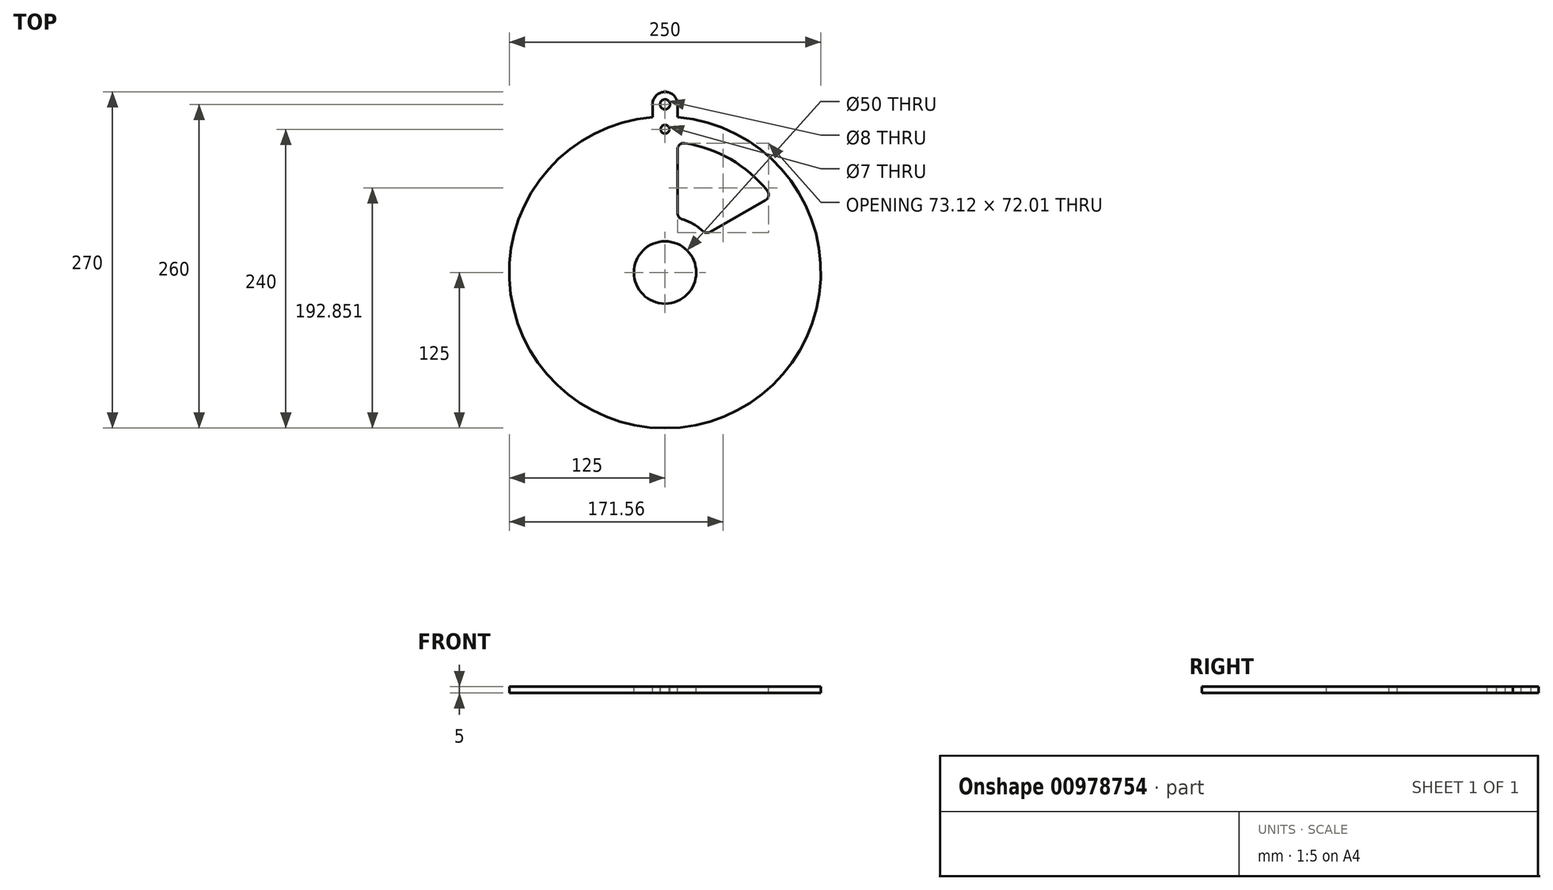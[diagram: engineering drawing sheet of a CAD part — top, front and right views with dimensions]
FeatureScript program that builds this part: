
annotation { "Feature Type Name" : "Feature", "Feature Type Description" : "" }
export const myFeature = defineFeature(function(context is Context, id is Id, definition is map)
    precondition{}
    {
        {
            var Q0;
            Q0=qCreatedBy(makeId("Top.planeOp"),FACE);
            var sketch = newSketch(context, id + "F0", { "sketchPlane" : qUnion([Q0])});
            skCircle(sketch, "E0", {"center": v(0, 0) * mm, "radius": 25 * mm});
            skSolve(sketch);
        }
        {
            var Q0;
            Q0=qCreatedBy(makeId("Top.planeOp"),FACE);
            var sketch = newSketch(context, id + "F1", { "sketchPlane" : qUnion([Q0])});
            skCircle(sketch, "E1", {"center": v(0, 0) * mm, "radius": 125 * mm});
            skSolve(sketch);
        }
        {
            var Q0;
            Q0=qCreatedBy(makeId("Top.planeOp"),FACE);
            var sketch = newSketch(context, id + "F2", { "sketchPlane" : qUnion([Q0])});
            skLineSegment(sketch, "E2", {"start": v(10, 98.87) * mm, "end": v(10, 47.7) * mm});
            skLineSegment(sketch, "E3", {"start": v(36.3, 32.5) * mm, "end": v(80.62, 58.1) * mm});
            skArc(sketch, "E4", {"start": v(82.03, 65.55) * mm, "mid": v(52.5, 90.93) * mm, "end": v(15.75, 103.81) * mm});
            skArc(sketch, "E5", {"start": v(30.43, 33.15) * mm, "mid": v(22.5, 38.97) * mm, "end": v(13.5, 42.93) * mm});
            skLineSegment(sketch, "E6", {"start": v(0, 0) * mm, "end": v(223.37, 128.96) * mm, "construction": true});
            skLineSegment(sketch, "E7", {"start": v(0, 0) * mm, "end": v(0, 140.53) * mm, "construction": true});
            skPoint(sketch, "E8.visualSharp", {"position": v(10, 104.52) * mm});
            skArc(sketch, "E8.filletArc", {"start": v(15.75, 103.81) * mm, "mid": v(11.74, 102.66) * mm, "end": v(10, 98.87) * mm});
            skPoint(sketch, "E9.visualSharp", {"position": v(85.52, 60.92) * mm});
            skArc(sketch, "E9.filletArc", {"start": v(80.62, 58.1) * mm, "mid": v(83.04, 61.5) * mm, "end": v(82.03, 65.55) * mm});
            skPoint(sketch, "E10.visualSharp", {"position": v(33, 30.6) * mm});
            skArc(sketch, "E10.filletArc", {"start": v(30.43, 33.15) * mm, "mid": v(33.26, 31.87) * mm, "end": v(36.3, 32.5) * mm});
            skPoint(sketch, "E11.visualSharp", {"position": v(10, 43.87) * mm});
            skArc(sketch, "E11.filletArc", {"start": v(10, 47.7) * mm, "mid": v(10.97, 44.74) * mm, "end": v(13.5, 42.93) * mm});
            skSolve(sketch);
        }
        {
            var Q0;
            Q0=qCreatedBy(makeId("Top.planeOp"),FACE);
            var sketch = newSketch(context, id + "F3", { "sketchPlane" : qUnion([Q0])});
            skLineSegment(sketch, "E12", {"start": v(-10, 120) * mm, "end": v(-10, 135) * mm});
            skArc(sketch, "E13", {"start": v(10, 135) * mm, "mid": v(0, 145) * mm, "end": v(-10, 135) * mm});
            skLineSegment(sketch, "E14", {"start": v(10, 135) * mm, "end": v(10, 120) * mm});
            skLineSegment(sketch, "E15", {"start": v(-10, 120) * mm, "end": v(10, 120) * mm});
            skSolve(sketch);
        }
        {
            var Q0;
            Q0=makeQuery(id+"F1.imprint","IMPRINT",FACE,{"disambiguationData":[TD([[makeQuery(id+"F1.imprint","IMPRINT",EDGE,{"derivedFrom":sQuery(id+"F1.wireOp",EDGE,"E1")}),1.0]])]});
            extrude(context, id + "F4", {"entities" : qUnion([Q0]), "oppositeDirection" : true, "depth" : 5 * mm, "offsetDistance" : 25 * mm});
        }
        {
            var Q0;
            Q0 = qSketchRegion(id + "F2", true);
            extrude(context, id + "F5", {"entities" : qUnion([Q0]), "operationType" : NewBodyOperationType.REMOVE, "endBound" : BoundingType.UP_TO_NEXT, "oppositeDirection" : true, "depth" : 25 * mm, "offsetDistance" : 25 * mm});
        }
        {
            var Q0;
            Q0=makeQuery(id+"F3.imprint","IMPRINT",FACE,{"disambiguationData":[TD([[makeQuery(id+"F3.imprint","IMPRINT",EDGE,{"derivedFrom":sQuery(id+"F3.wireOp",EDGE,"E12")}),-1.0]])]});
            var Q1;
            Q1=makeQuery(id+"F4.opExtrude","CAP_FACE",FACE,{"disambiguationData":[OSD([sQuery(id+"F1.wireOp",EDGE,"E1")])],"isStart":false});
            extrude(context, id + "F6", {"entities" : qUnion([Q0]), "operationType" : NewBodyOperationType.ADD, "endBound" : BoundingType.UP_TO_SURFACE, "oppositeDirection" : true, "depth" : 25 * mm, "endBoundEntityFace" : qUnion([Q1]), "offsetDistance" : 25 * mm});
        }
        {
            var Q0;
            Q0=makeQuery(id+"F0.imprint","IMPRINT",FACE,{"disambiguationData":[TD([[makeQuery(id+"F0.imprint","IMPRINT",EDGE,{"derivedFrom":sQuery(id+"F0.wireOp",EDGE,"E0")}),1.0]])]});
            extrude(context, id + "F7", {"entities" : qUnion([Q0]), "operationType" : NewBodyOperationType.REMOVE, "oppositeDirection" : true, "depth" : 25 * mm, "offsetDistance" : 25 * mm});
        }
        {
            var Q0;
            Q0=qCreatedBy(makeId("Top.planeOp"),FACE);
            var sketch = newSketch(context, id + "F8", { "sketchPlane" : qUnion([Q0])});
            skCircle(sketch, "E16", {"center": v(0, 135) * mm, "radius": 4 * mm});
            skSolve(sketch);
        }
        {
            var Q0;
            Q0 = qSketchRegion(id + "F8", true);
            extrude(context, id + "F9", {"entities" : qUnion([Q0]), "operationType" : NewBodyOperationType.REMOVE, "endBound" : BoundingType.UP_TO_NEXT, "oppositeDirection" : true, "depth" : 25 * mm, "offsetDistance" : 25 * mm});
        }
        {
            var Q0;
            Q0=qCreatedBy(makeId("Top.planeOp"),FACE);
            var sketch = newSketch(context, id + "F10", { "sketchPlane" : qUnion([Q0])});
            skCircle(sketch, "E17", {"center": v(0, 115) * mm, "radius": 3.5 * mm});
            skSolve(sketch);
        }
        {
            var Q0;
            Q0=makeQuery(id+"F10.imprint","IMPRINT",FACE,{"disambiguationData":[TD([[makeQuery(id+"F10.imprint","IMPRINT",EDGE,{"derivedFrom":sQuery(id+"F10.wireOp",EDGE,"E17")}),1.0]])]});
            extrude(context, id + "F11", {"entities" : qUnion([Q0]), "operationType" : NewBodyOperationType.REMOVE, "endBound" : BoundingType.UP_TO_NEXT, "oppositeDirection" : true, "depth" : 25 * mm, "offsetDistance" : 25 * mm});
        }
    });
